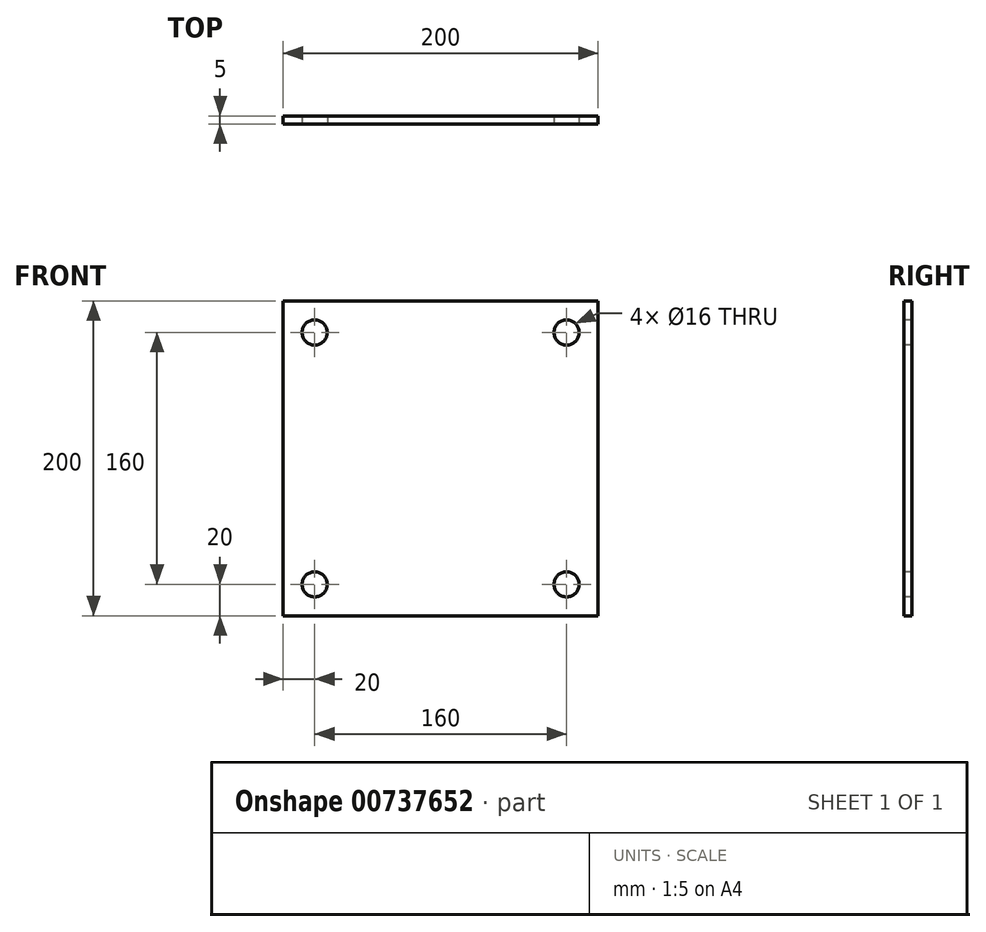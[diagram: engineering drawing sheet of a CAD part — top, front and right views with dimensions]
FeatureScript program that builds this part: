
annotation { "Feature Type Name" : "Feature", "Feature Type Description" : "" }
export const myFeature = defineFeature(function(context is Context, id is Id, definition is map)
    precondition{}
    {
        {
            var Q0;
            Q0=qCreatedBy(makeId("Front.planeOp"),FACE);
            var sketch = newSketch(context, id + "F0", { "sketchPlane" : qUnion([Q0])});
            skLineSegment(sketch, "E0.bottom", {"start": v(-100, 100) * mm, "end": v(100, 100) * mm});
            skLineSegment(sketch, "E0.top", {"start": v(-100, -100) * mm, "end": v(100, -100) * mm});
            skLineSegment(sketch, "E0.left", {"start": v(-100, 100) * mm, "end": v(-100, -100) * mm});
            skLineSegment(sketch, "E0.right", {"start": v(100, 100) * mm, "end": v(100, -100) * mm});
            skSolve(sketch);
        }
        {
            var Q0;
            Q0=makeQuery(id+"F0.imprint","IMPRINT",FACE,{"disambiguationData":[TD([[makeQuery(id+"F0.imprint","IMPRINT",EDGE,{"derivedFrom":sQuery(id+"F0.wireOp",EDGE,"E0.bottom")}),-1.0]])]});
            extrude(context, id + "F1", {"entities" : qUnion([Q0]), "endBound" : BoundingType.SYMMETRIC, "depth" : 5 * mm, "offsetDistance" : 25 * mm});
        }
        {
            var Q0;
            Q0=makeQuery(id+"F1.opExtrude","CAP_FACE",FACE,{"disambiguationData":[OSD([sQuery(id+"F0.wireOp",EDGE,"E0.bottom"),sQuery(id+"F0.wireOp",EDGE,"E0.top"),sQuery(id+"F0.wireOp",EDGE,"E0.left"),sQuery(id+"F0.wireOp",EDGE,"E0.right")])],"isStart":false});
            var sketch = newSketch(context, id + "F2", { "sketchPlane" : qUnion([Q0])});
            skCircle(sketch, "E1", {"center": v(-80, 80) * mm, "radius": 8 * mm});
            skCircle(sketch, "E2", {"center": v(80, 80) * mm, "radius": 8 * mm});
            skCircle(sketch, "E3", {"center": v(80, -80) * mm, "radius": 8 * mm});
            skCircle(sketch, "E4", {"center": v(-80, -80) * mm, "radius": 8 * mm});
            skSolve(sketch);
        }
        {
            var Q0;
            Q0 = qSketchRegion(id + "F2", true);
            extrude(context, id + "F3", {"entities" : qUnion([Q0]), "operationType" : NewBodyOperationType.REMOVE, "endBound" : BoundingType.THROUGH_ALL, "oppositeDirection" : true, "depth" : 25 * mm, "offsetDistance" : 25 * mm});
        }
    });
